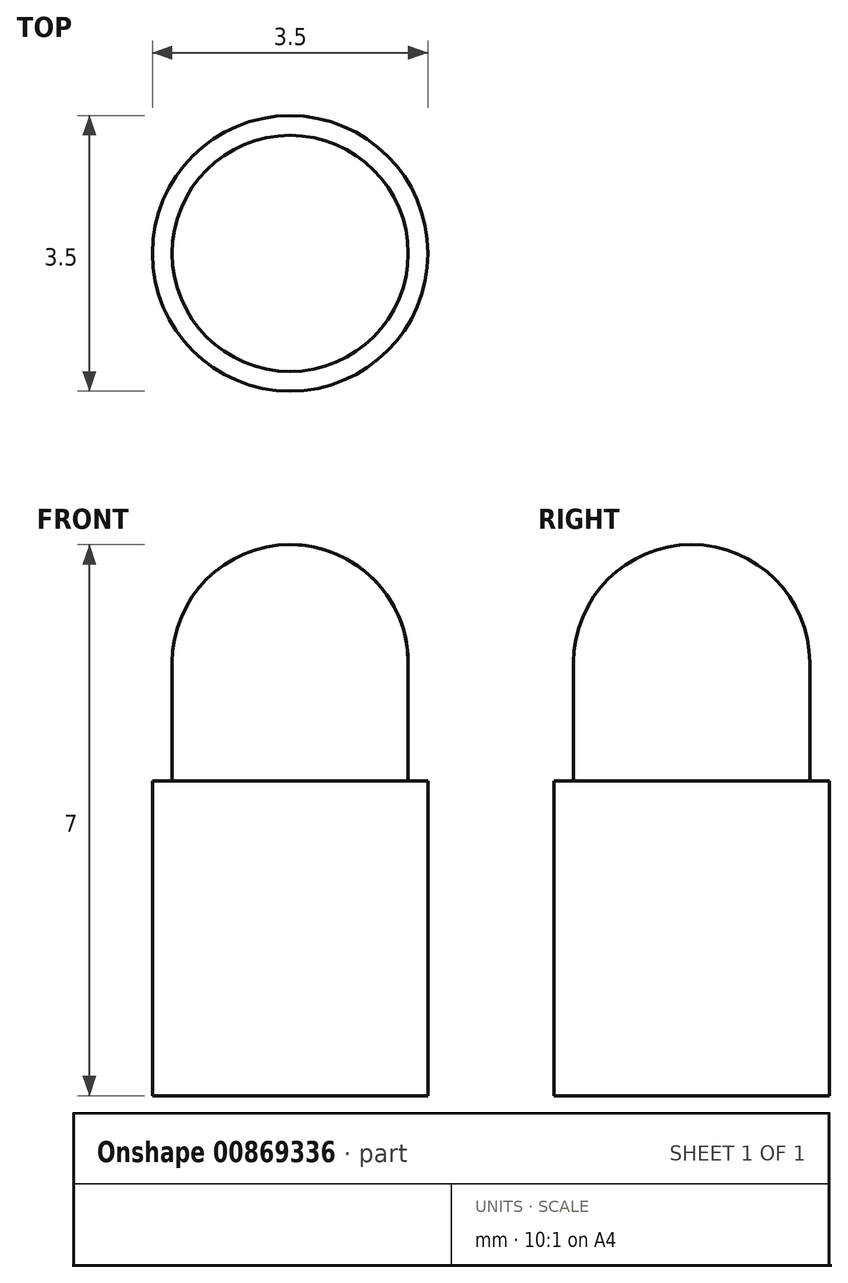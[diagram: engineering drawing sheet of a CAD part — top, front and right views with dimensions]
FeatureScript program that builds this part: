
annotation { "Feature Type Name" : "Feature", "Feature Type Description" : "" }
export const myFeature = defineFeature(function(context is Context, id is Id, definition is map)
    precondition{}
    {
        {
            var Q0;
            Q0=qCreatedBy(makeId("Front.planeOp"),FACE);
            var sketch = newSketch(context, id + "F0", { "sketchPlane" : qUnion([Q0])});
            skArc(sketch, "E0", {"start": v(0, 1.5) * mm, "mid": v(-1.06, 1.06) * mm, "end": v(-1.5, 0) * mm});
            skLineSegment(sketch, "E1", {"start": v(-1.75, -5.5) * mm, "end": v(0, -5.5) * mm});
            skLineSegment(sketch, "E2", {"start": v(0, -5.5) * mm, "end": v(0, 1.5) * mm});
            skLineSegment(sketch, "E3", {"start": v(-1.5, 0) * mm, "end": v(-1.5, -1.5) * mm});
            skLineSegment(sketch, "E4", {"start": v(-1.5, -1.5) * mm, "end": v(-1.75, -1.5) * mm});
            skLineSegment(sketch, "E5", {"start": v(-1.75, -5.5) * mm, "end": v(-1.75, -1.5) * mm});
            skSolve(sketch);
        }
        {
            var Q0;
            Q0=makeQuery(id+"F0.imprint","IMPRINT",FACE,{"disambiguationData":[TD([[makeQuery(id+"F0.imprint","IMPRINT",EDGE,{"derivedFrom":sQuery(id+"F0.wireOp",EDGE,"E0")}),1.0]])]});
            var Q1;
            Q1=sQuery(id+"F0.wireOp",EDGE,"E2");
            revolve(context, id + "F1", {"surfaceOperationType" : NewSurfaceOperationType.NEW, "entities" : qUnion([Q0]), "axis" : qUnion([Q1]), "revolveType" : RevolveType.FULL});
        }
    });
